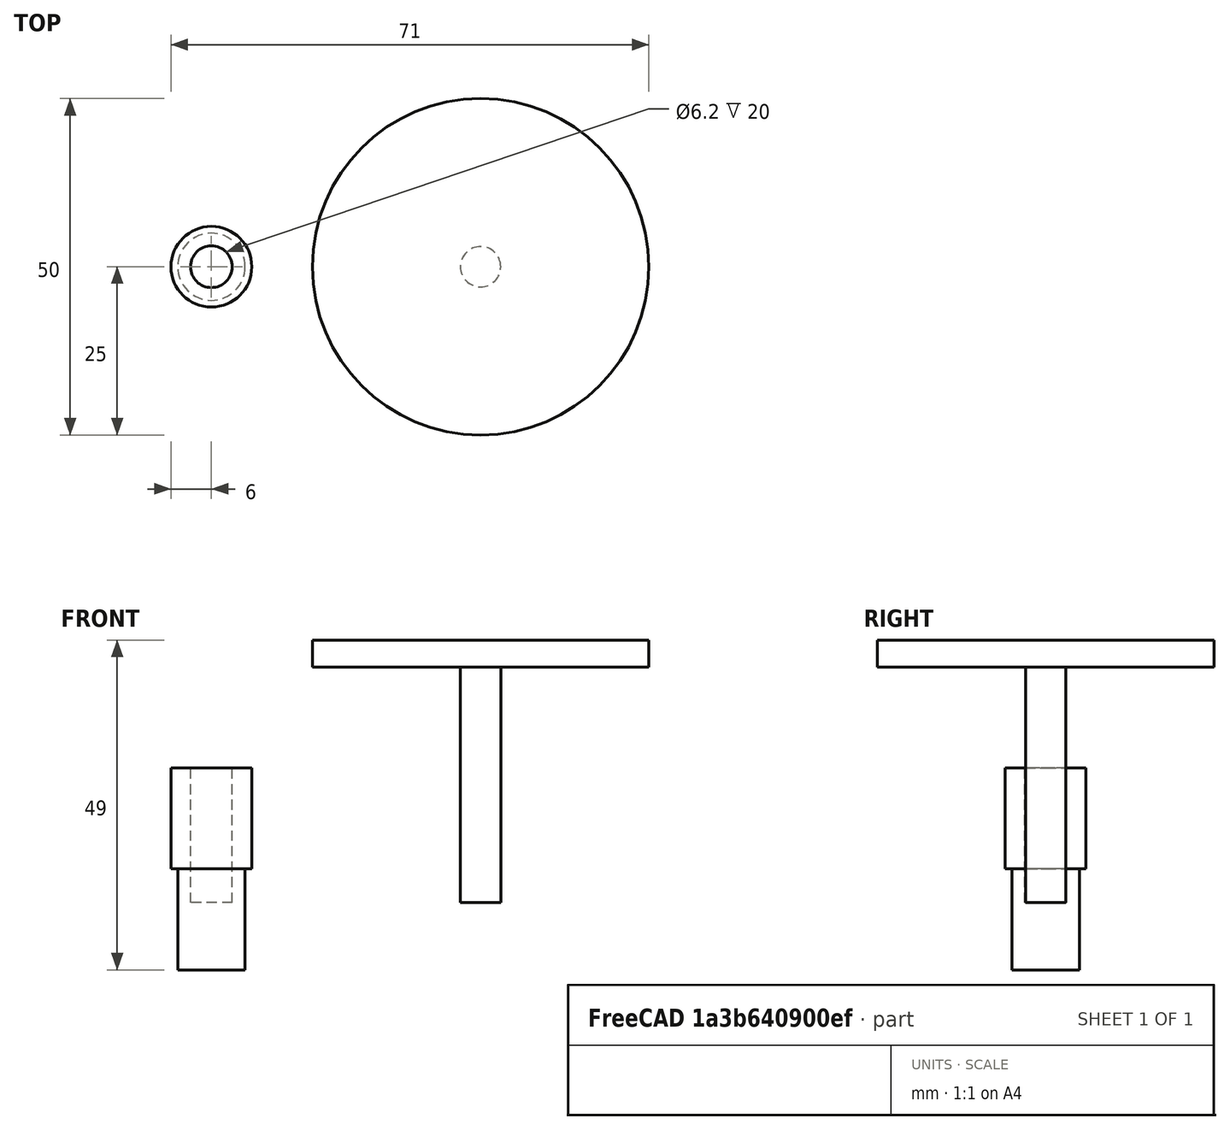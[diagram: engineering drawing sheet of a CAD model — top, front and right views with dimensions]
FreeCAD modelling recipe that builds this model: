
FCSTD DOCUMENT  (FreeCAD 0.14R3702 (Git))
Label: shaft_2_interlocking
License: CC-BY 3.0
LicenseURL: http://creativecommons.org/licenses/by/3.0/
objects: Part::Cylinder×6, Part::Cut×3, Part::MultiFuse×1
note: 10 computed .brp shape members not serialized (recipe doc carries the construction recipe); baked Part::Feature solids carry a one-line shape summary decoded from their .brp

FEATURE [Part::Cylinder] Cylinder
  Angle = 360
  Height = 30
  Radius = 6
FEATURE [Part::Cylinder] Cylinder001
  Angle = 360
  Height = 20
  Placement = pos=(0,0,10) rot=(0,0,1;0rad)
  Radius = 3.1
FEATURE [Part::Cylinder] Cylinder002
  Angle = 360
  Height = 35
  Placement = pos=(40,0,50) rot=(0,0,1;0rad)
  Radius = 3
FEATURE [Part::Cylinder] Cylinder003
  Angle = 360
  Height = 4
  Placement = pos=(40,0,85) rot=(0,0,1;0rad)
  Radius = 25
FEATURE [Part::Cut] Cut
  Base = -> Cylinder
  Tool = -> Cylinder001
FEATURE [Part::Cylinder] Cylinder004
  Angle = 360
  Height = 15
  Placement = pos=(-20,0,0) rot=(0,0,1;0rad)
  Radius = 6
FEATURE [Part::Cylinder] Cylinder005
  Angle = 360
  Height = 15
  Placement = pos=(-20,0,0) rot=(0,0,1;0rad)
  Radius = 5
FEATURE [Part::Cut] Cut001
  Base = -> Cylinder004
  Placement = pos=(20,0,0) rot=(0,0,1;0rad)
  Tool = -> Cylinder005
FEATURE [Part::Cut] Cut002
  Base = -> Cut
  Tool = -> Cut001
FEATURE [Part::MultiFuse] Fusion
  Placement = pos=(0,0,-40) rot=(0,0,1;0rad)
  Shapes = -> [Cylinder003,Cylinder002]
